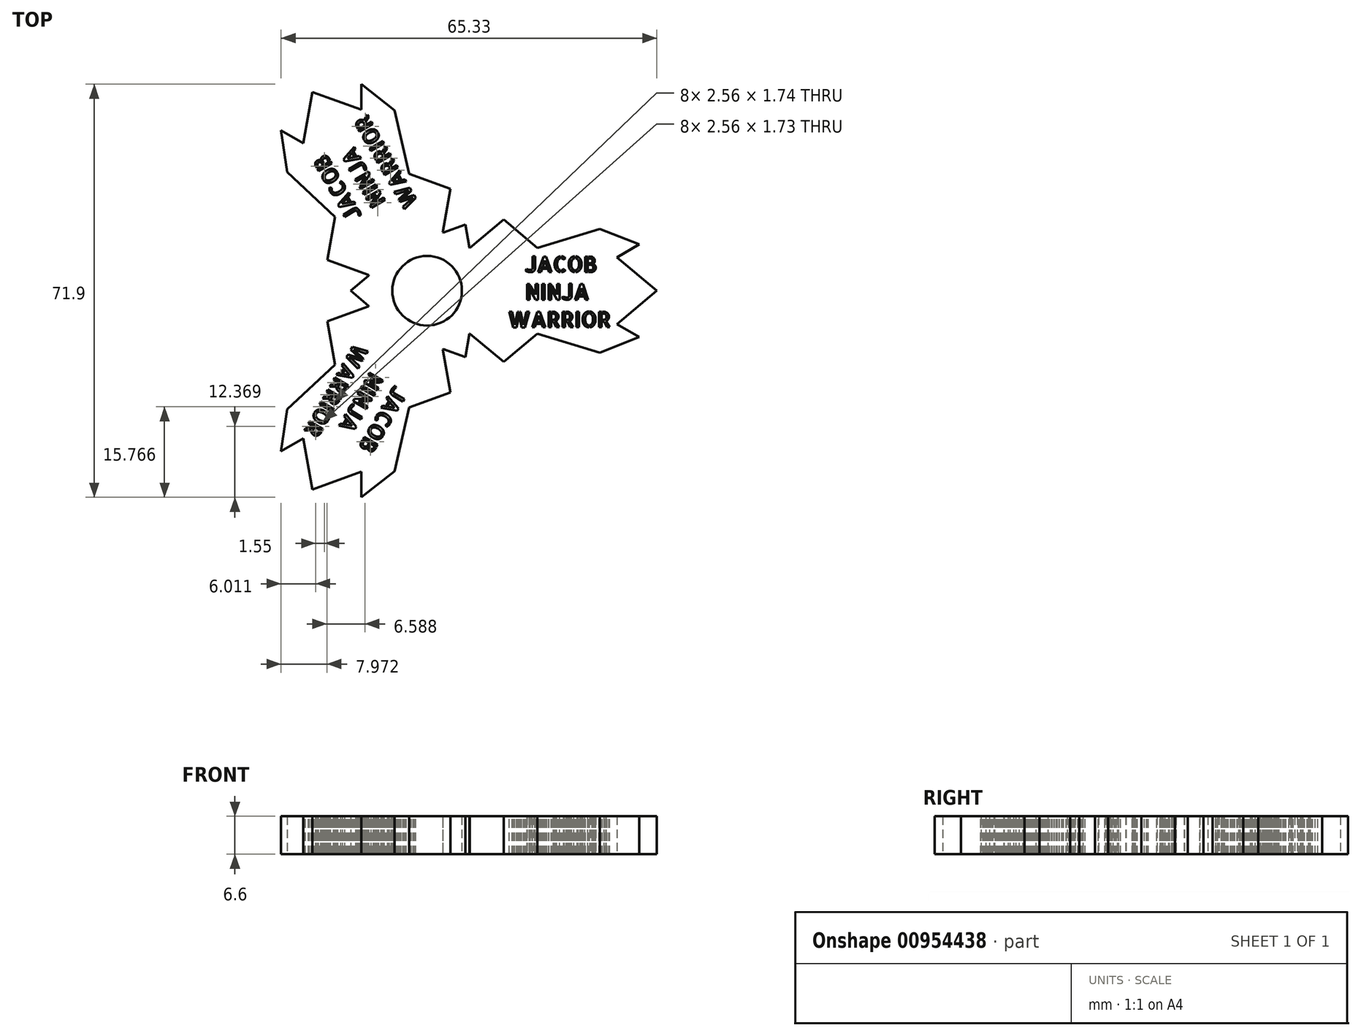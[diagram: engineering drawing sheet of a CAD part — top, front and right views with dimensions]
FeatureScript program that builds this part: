
annotation { "Feature Type Name" : "Feature", "Feature Type Description" : "" }
export const myFeature = defineFeature(function(context is Context, id is Id, definition is map)
    precondition{}
    {
        {
            var Q0;
            Q0=qCreatedBy(makeId("Top.planeOp"),FACE);
            var sketch = newSketch(context, id + "F0", { "sketchPlane" : qUnion([Q0])});
            skCircle(sketch, "E0", {"center": v(0, 0) * mm, "radius": 11 * mm});
            skLineSegment(sketch, "E1", {"start": v(34.84, -13.55) * mm, "end": v(54.62, -19.59) * mm});
            skLineSegment(sketch, "E2", {"start": v(0, 0) * mm, "end": v(55.57, 0) * mm, "construction": true});
            skLineSegment(sketch, "E3.MirrorCS", {"start": v(34.84, 13.55) * mm, "end": v(54.62, 19.59) * mm});
            skLineSegment(sketch, "E4", {"start": v(13.54, 13.55) * mm, "end": v(24.2, 22.5) * mm});
            skLineSegment(sketch, "E5", {"start": v(24.2, 22.5) * mm, "end": v(34.84, 13.55) * mm});
            skLineSegment(sketch, "E6.MirrorCS", {"start": v(13.54, -13.55) * mm, "end": v(24.2, -22.5) * mm});
            skLineSegment(sketch, "E7.MirrorCS", {"start": v(24.2, -22.5) * mm, "end": v(34.84, -13.55) * mm});
            skLineSegment(sketch, "E8", {"start": v(54.62, -19.59) * mm, "end": v(67.02, -14.64) * mm});
            skLineSegment(sketch, "E9", {"start": v(67.02, -14.64) * mm, "end": v(60.03, -10.57) * mm});
            skLineSegment(sketch, "E10", {"start": v(60.03, -10.57) * mm, "end": v(72.6, 0) * mm});
            skLineSegment(sketch, "E11", {"start": v(72.6, 0) * mm, "end": v(55.57, 0) * mm, "construction": true});
            skLineSegment(sketch, "E12.MirrorCS", {"start": v(60.03, 10.57) * mm, "end": v(72.6, 0) * mm});
            skLineSegment(sketch, "E13.MirrorCS", {"start": v(54.62, 19.59) * mm, "end": v(67.02, 14.64) * mm});
            skLineSegment(sketch, "E14.MirrorCS", {"start": v(67.02, 14.64) * mm, "end": v(60.03, 10.57) * mm});
            skLineSegment(sketch, "E15", {"start": v(24.2, 22.5) * mm, "end": v(24.2, -22.5) * mm, "construction": true});
            skLineSegment(sketch, "E16.MirrorCS", {"start": v(13.57, 13.55) * mm, "end": v(-6.2, 19.59) * mm});
            skLineSegment(sketch, "E17.MirrorCS", {"start": v(-6.2, 19.59) * mm, "end": v(-18.6, 14.64) * mm});
            skLineSegment(sketch, "E18.MirrorCS", {"start": v(-18.6, 14.64) * mm, "end": v(-11.62, 10.57) * mm});
            skLineSegment(sketch, "E19.MirrorCS", {"start": v(-11.62, 10.57) * mm, "end": v(-24.2, 0) * mm});
            skLineSegment(sketch, "E20.MirrorCS", {"start": v(-11.62, -10.57) * mm, "end": v(-24.2, 0) * mm});
            skLineSegment(sketch, "E21.MirrorCS", {"start": v(-18.6, -14.64) * mm, "end": v(-11.62, -10.57) * mm});
            skLineSegment(sketch, "E22.MirrorCS", {"start": v(-6.2, -19.59) * mm, "end": v(-18.6, -14.64) * mm});
            skLineSegment(sketch, "E23.MirrorCS", {"start": v(13.57, -13.55) * mm, "end": v(-6.2, -19.59) * mm});
            skLineSegment(sketch, "E24.MirrorCS", {"start": v(-24.2, 0) * mm, "end": v(-7.16, 0) * mm, "construction": true});
            skPoint(sketch, "E25", {"position": v(19.43, 0) * mm});
            skSolve(sketch);
        }
        {
            var Q0;
            Q0 = qSketchRegion(id + "F0", true);
            extrude(context, id + "F1", {"entities" : qUnion([Q0]), "endBound" : BoundingType.SYMMETRIC, "depth" : 12 * mm, "offsetDistance" : 25 * mm});
        }
        {
            var Q0;
            Q0=makeQuery(id+"F1.opExtrude","SWEPT_BODY",BODY,{"disambiguationData":[OSD([sQuery(id+"F0.wireOp",EDGE,"E0"),sQuery(id+"F0.wireOp",EDGE,"E1"),sQuery(id+"F0.wireOp",EDGE,"E3.MirrorCS"),sQuery(id+"F0.wireOp",EDGE,"E4"),sQuery(id+"F0.wireOp",EDGE,"E5"),sQuery(id+"F0.wireOp",EDGE,"E6.MirrorCS"),sQuery(id+"F0.wireOp",EDGE,"E7.MirrorCS"),sQuery(id+"F0.wireOp",EDGE,"E8"),sQuery(id+"F0.wireOp",EDGE,"E9"),sQuery(id+"F0.wireOp",EDGE,"E10"),sQuery(id+"F0.wireOp",EDGE,"E12.MirrorCS"),sQuery(id+"F0.wireOp",EDGE,"E13.MirrorCS"),sQuery(id+"F0.wireOp",EDGE,"E14.MirrorCS"),sQuery(id+"F0.wireOp",EDGE,"E16.MirrorCS"),sQuery(id+"F0.wireOp",EDGE,"E17.MirrorCS"),sQuery(id+"F0.wireOp",EDGE,"E18.MirrorCS"),sQuery(id+"F0.wireOp",EDGE,"E19.MirrorCS"),sQuery(id+"F0.wireOp",EDGE,"E20.MirrorCS"),sQuery(id+"F0.wireOp",EDGE,"E21.MirrorCS"),sQuery(id+"F0.wireOp",EDGE,"E22.MirrorCS"),sQuery(id+"F0.wireOp",EDGE,"E23.MirrorCS")])]});
            var Q1;
            Q1=sQuery(id+"F0.wireOp",VERTEX,"E2.start");
            transform(context, id + "F2", {"entities" : qUnion([Q0]), "transformType" : TransformType.SCALE_UNIFORMLY, "scale" : .55, "scalePoint" : qUnion([Q1]), "makeCopy" : false});
        }
        {
            var Q0;
            {var subQ0=makeQuery(id+"F1.opExtrude","CAP_FACE",FACE,{"disambiguationData":[OSD([sQuery(id+"F0.wireOp",EDGE,"E0"),sQuery(id+"F0.wireOp",EDGE,"E1"),sQuery(id+"F0.wireOp",EDGE,"E3.MirrorCS"),sQuery(id+"F0.wireOp",EDGE,"E4"),sQuery(id+"F0.wireOp",EDGE,"E5"),sQuery(id+"F0.wireOp",EDGE,"E6.MirrorCS"),sQuery(id+"F0.wireOp",EDGE,"E7.MirrorCS"),sQuery(id+"F0.wireOp",EDGE,"E8"),sQuery(id+"F0.wireOp",EDGE,"E9"),sQuery(id+"F0.wireOp",EDGE,"E10"),sQuery(id+"F0.wireOp",EDGE,"E12.MirrorCS"),sQuery(id+"F0.wireOp",EDGE,"E13.MirrorCS"),sQuery(id+"F0.wireOp",EDGE,"E14.MirrorCS"),sQuery(id+"F0.wireOp",EDGE,"E16.MirrorCS"),sQuery(id+"F0.wireOp",EDGE,"E17.MirrorCS"),sQuery(id+"F0.wireOp",EDGE,"E18.MirrorCS"),sQuery(id+"F0.wireOp",EDGE,"E19.MirrorCS"),sQuery(id+"F0.wireOp",EDGE,"E20.MirrorCS"),sQuery(id+"F0.wireOp",EDGE,"E21.MirrorCS"),sQuery(id+"F0.wireOp",EDGE,"E22.MirrorCS"),sQuery(id+"F0.wireOp",EDGE,"E23.MirrorCS")])],"isStart":false});Q0=makeQuery(id+"F5.boolean.opBoolean","MERGE",FACE,{"derivedFrom":[subQ0,makeQuery(id+"F5.opPattern","COPY",FACE,{"derivedFrom":subQ0,"instanceName":"1"}),makeQuery(id+"F5.opPattern","COPY",FACE,{"derivedFrom":subQ0,"instanceName":"2"})]});}
            var sketch = newSketch(context, id + "F3", { "sketchPlane" : qUnion([Q0])});
            skText(sketch, "E26", { "text": "   JACOB\n   NINJA\nWARRIOR", "fontName": "AllertaStencil-Regular.ttf"});
            const initialGuessF3  = {"E26": [0.01401, 0.00325, 1, 0, 0.0027]};
            skSetInitialGuess(sketch, initialGuessF3);
            skSolve(sketch);
        }
        {
            var Q0;
            Q0 = qSketchRegion(id + "F3", true);
            extrude(context, id + "F4", {"entities" : qUnion([Q0]), "operationType" : NewBodyOperationType.REMOVE, "endBound" : BoundingType.THROUGH_ALL, "oppositeDirection" : true, "depth" : 25 * mm, "offsetDistance" : 25 * mm});
        }
        {
            var Q0;
            Q0=makeQuery(id+"F1.opExtrude","SWEPT_BODY",BODY,{"disambiguationData":[OSD([sQuery(id+"F0.wireOp",EDGE,"E0"),sQuery(id+"F0.wireOp",EDGE,"djJdUprO-JuXV-0RCn-O7Da-CJFyRceKIc5y"),sQuery(id+"F0.wireOp",EDGE,"hrFff61V-yzU9-w8OY-s0KU-PMaDHwhZ1WZ4"),sQuery(id+"F0.wireOp",EDGE,"U4PsKhP8-V5aI-PSWf-MWyq-uZGt5TfwTbuY"),sQuery(id+"F0.wireOp",EDGE,"H5MN2mBR-xtjV-F9cl-VUFH-70YQBbGMt8cF")])]});
            var Q1;
            Q1=makeQuery(id+"F1.opExtrude","CAP_EDGE",EDGE,{"disambiguationData":[OSD([sQuery(id+"F0.wireOp",EDGE,"E0")])],"isStart":false});
            circularPattern(context, id + "F5", {"operationType" : NewBodyOperationType.ADD, "entities" : qUnion([Q0]), "axis" : qUnion([Q1]), "angle" : 360 * degree, "instanceCount" : 3, "equalSpace" : true});
        }
    });
